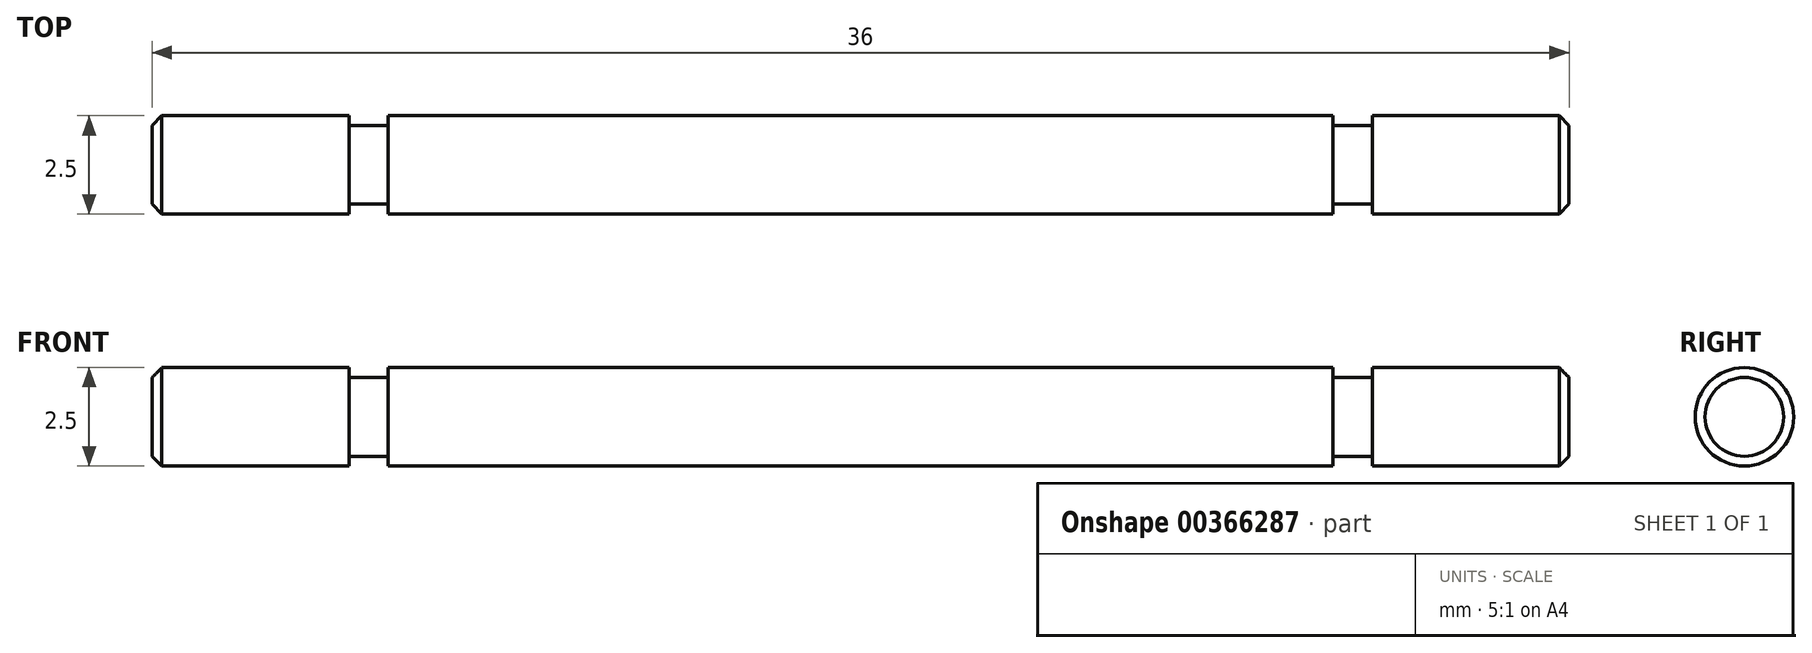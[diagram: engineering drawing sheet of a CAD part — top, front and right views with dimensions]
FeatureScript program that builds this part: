
annotation { "Feature Type Name" : "Feature", "Feature Type Description" : "" }
export const myFeature = defineFeature(function(context is Context, id is Id, definition is map)
    precondition{}
    {
        {
            var Q0;
            Q0=qCreatedBy(makeId("Front.planeOp"),FACE);
            var sketch = newSketch(context, id + "F0", { "sketchPlane" : qUnion([Q0])});
            skLineSegment(sketch, "E0", {"start": v(98.8, 45.62) * mm, "end": v(98.8, 46.87) * mm});
            skLineSegment(sketch, "E1", {"start": v(98.8, 46.87) * mm, "end": v(93.8, 46.87) * mm});
            skLineSegment(sketch, "E2", {"start": v(93.8, 46.87) * mm, "end": v(93.8, 46.62) * mm});
            skLineSegment(sketch, "E3", {"start": v(93.8, 46.62) * mm, "end": v(92.8, 46.62) * mm});
            skLineSegment(sketch, "E4", {"start": v(92.8, 46.62) * mm, "end": v(92.8, 46.87) * mm});
            skLineSegment(sketch, "E5", {"start": v(92.8, 46.87) * mm, "end": v(80.8, 46.87) * mm});
            skLineSegment(sketch, "E6", {"start": v(80.8, 46.87) * mm, "end": v(80.8, 45.62) * mm});
            skLineSegment(sketch, "E7", {"start": v(80.8, 45.62) * mm, "end": v(98.8, 45.62) * mm});
            skLineSegment(sketch, "E8.MirrorCS", {"start": v(67.8, 46.87) * mm, "end": v(67.8, 46.62) * mm});
            skLineSegment(sketch, "E9.MirrorCS", {"start": v(67.8, 46.62) * mm, "end": v(68.8, 46.62) * mm});
            skLineSegment(sketch, "E10.MirrorCS", {"start": v(62.8, 45.62) * mm, "end": v(62.8, 46.87) * mm});
            skLineSegment(sketch, "E11.MirrorCS", {"start": v(68.8, 46.62) * mm, "end": v(68.8, 46.87) * mm});
            skLineSegment(sketch, "E12.MirrorCS", {"start": v(62.8, 46.87) * mm, "end": v(67.8, 46.87) * mm});
            skLineSegment(sketch, "E13.MirrorCS", {"start": v(80.8, 45.62) * mm, "end": v(62.8, 45.62) * mm});
            skLineSegment(sketch, "E14.MirrorCS", {"start": v(68.8, 46.87) * mm, "end": v(80.8, 46.87) * mm});
            skSolve(sketch);
        }
        {
            var Q0;
            Q0=makeQuery(id+"F0.imprint","IMPRINT",FACE,{"disambiguationData":[TD([[makeQuery(id+"F0.imprint","IMPRINT",EDGE,{"derivedFrom":sQuery(id+"F0.wireOp",EDGE,"E0")}),1.0]])]});
            var Q1;
            Q1=makeQuery(id+"F0.imprint","IMPRINT",FACE,{"disambiguationData":[TD([[makeQuery(id+"F0.imprint","IMPRINT",EDGE,{"derivedFrom":sQuery(id+"F0.wireOp",EDGE,"E6")}),-1.0]])]});
            var Q2;
            Q2=sQuery(id+"F0.wireOp",EDGE,"E7");
            revolve(context, id + "F1", {"entities" : qUnion([Q0, Q1]), "axis" : qUnion([Q2]), "revolveType" : RevolveType.FULL});
        }
        {
            var Q0;
            Q0=makeQuery(id+"F1.opRevolve","SWEPT_EDGE",EDGE,{"disambiguationData":[OSD([sQuery(id+"F0.wireOp",EDGE,"E0"),sQuery(id+"F0.wireOp",EDGE,"E1")])]});
            var Q1;
            Q1=makeQuery(id+"F1.opRevolve","SWEPT_EDGE",EDGE,{"disambiguationData":[OSD([sQuery(id+"F0.wireOp",EDGE,"E10.MirrorCS"),sQuery(id+"F0.wireOp",EDGE,"E12.MirrorCS")])]});
            chamfer(context, id + "F2", {"entities" : qUnion([Q0, Q1]), "width" : 0.25 * mm, "tangentPropagation" : true});
        }
    });
